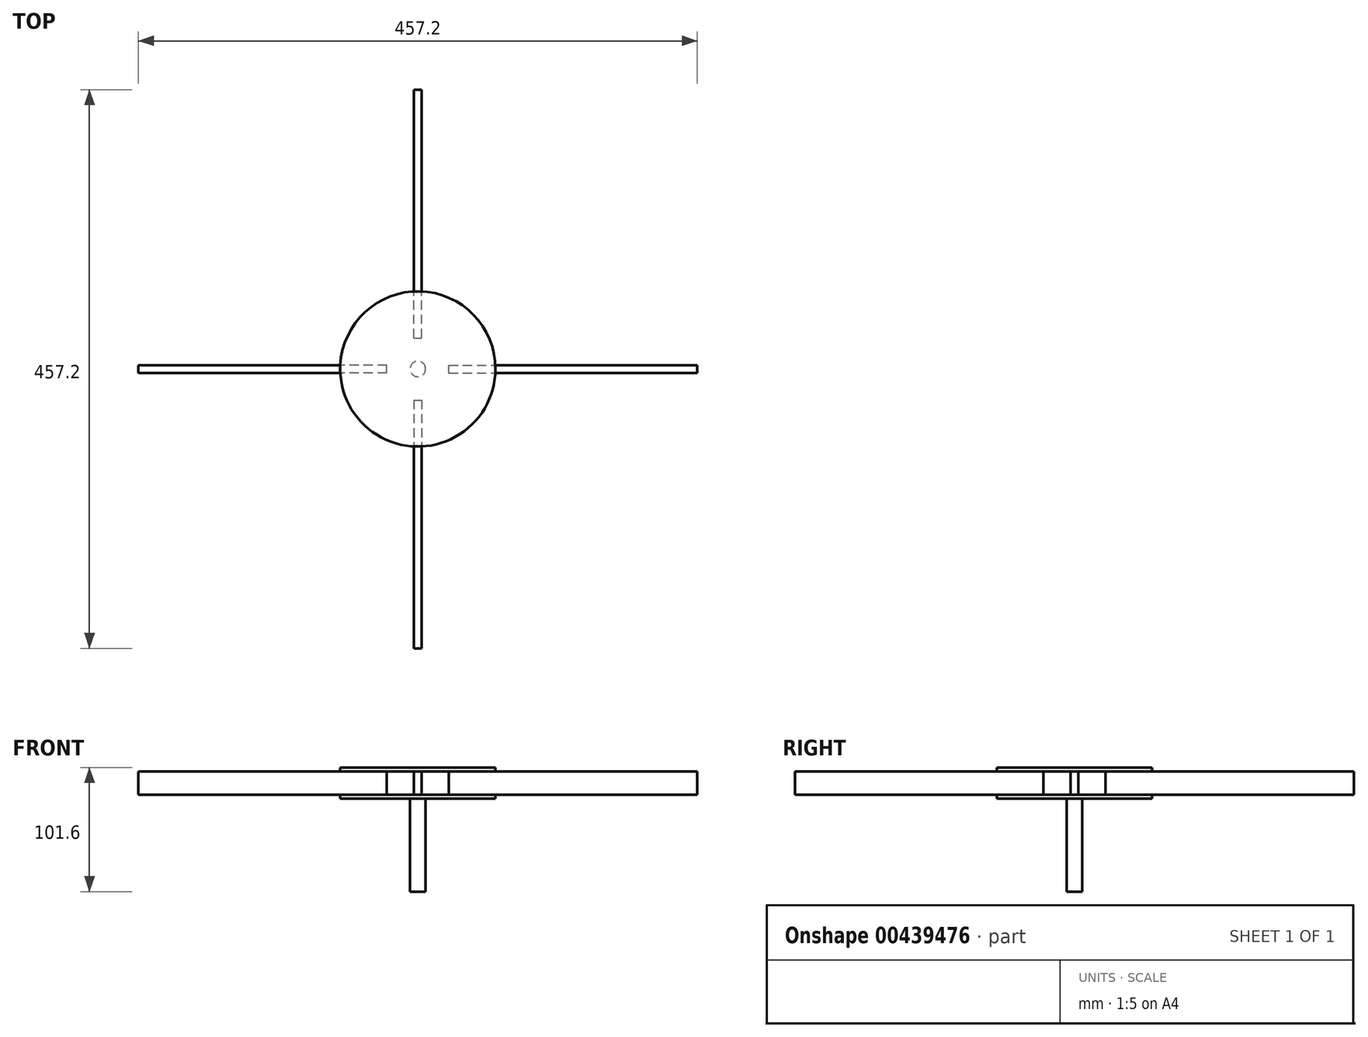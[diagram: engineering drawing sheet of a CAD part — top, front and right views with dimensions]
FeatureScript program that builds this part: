
annotation { "Feature Type Name" : "Feature", "Feature Type Description" : "" }
export const myFeature = defineFeature(function(context is Context, id is Id, definition is map)
    precondition{}
    {
        {
            var Q0;
            Q0=qCreatedBy(makeId("Top.planeOp"),FACE);
            var sketch = newSketch(context, id + "F0", { "sketchPlane" : qUnion([Q0])});
            skCircle(sketch, "E0", {"center": v(0, 0) * mm, "radius": 6.35 * mm});
            skSolve(sketch);
        }
        {
            var Q0;
            Q0=makeQuery(id+"F0.imprint","IMPRINT",FACE,{"disambiguationData":[TD([[makeQuery(id+"F0.imprint","IMPRINT",EDGE,{"derivedFrom":sQuery(id+"F0.wireOp",EDGE,"E0")}),1.0]])]});
            extrude(context, id + "F1", {"entities" : qUnion([Q0]), "endBound" : BoundingType.SYMMETRIC, "depth" : 76.2 * mm});
        }
        {
            var Q0;
            Q0=makeQuery(id+"F1.opExtrude","CAP_FACE",FACE,{"disambiguationData":[OSD([sQuery(id+"F0.wireOp",EDGE,"E0")])],"isStart":false});
            var sketch = newSketch(context, id + "F2", { "sketchPlane" : qUnion([Q0])});
            skCircle(sketch, "E1", {"center": v(0, 0) * mm, "radius": 63.5 * mm});
            skSolve(sketch);
        }
        {
            var Q0;
            Q0 = qSketchRegion(id + "F2", true);
            extrude(context, id + "F3", {"entities" : qUnion([Q0]), "operationType" : NewBodyOperationType.ADD, "depth" : 3.17 * mm});
        }
        {
            var Q0;
            Q0=makeQuery(id+"F3.opExtrude","CAP_FACE",FACE,{"disambiguationData":[OSD([sQuery(id+"F2.wireOp",EDGE,"E1")])],"isStart":false});
            var sketch = newSketch(context, id + "F4", { "sketchPlane" : qUnion([Q0])});
            skLineSegment(sketch, "E2.bottom", {"start": v(-3.17, 25.4) * mm, "end": v(3.18, 25.4) * mm});
            skLineSegment(sketch, "E2.top", {"start": v(-3.18, 228.6) * mm, "end": v(3.17, 228.6) * mm});
            skLineSegment(sketch, "E2.left", {"start": v(-3.17, 25.4) * mm, "end": v(-3.18, 228.6) * mm});
            skLineSegment(sketch, "E2.right", {"start": v(3.18, 25.4) * mm, "end": v(3.17, 228.6) * mm});
            skLineSegment(sketch, "E3.bottom", {"start": v(-25.4, -3.18) * mm, "end": v(-228.6, -3.18) * mm});
            skLineSegment(sketch, "E3.top", {"start": v(-25.4, 3.17) * mm, "end": v(-228.6, 3.17) * mm});
            skLineSegment(sketch, "E3.left", {"start": v(-25.4, -3.18) * mm, "end": v(-25.4, 3.17) * mm});
            skLineSegment(sketch, "E3.right", {"start": v(-228.6, -3.18) * mm, "end": v(-228.6, 3.17) * mm});
            skLineSegment(sketch, "E4", {"start": v(0, 63.5) * mm, "end": v(0, -63.5) * mm, "construction": true});
            skLineSegment(sketch, "E5", {"start": v(63.5, 0) * mm, "end": v(-63.5, 0) * mm, "construction": true});
            skPoint(sketch, "E6", {"position": v(-25.4, 0) * mm});
            skPoint(sketch, "E7", {"position": v(0, 25.4) * mm});
            skLineSegment(sketch, "E8.MirrorCS", {"start": v(25.4, -3.18) * mm, "end": v(25.4, 3.17) * mm});
            skLineSegment(sketch, "E9.MirrorCS", {"start": v(228.6, -3.17) * mm, "end": v(228.6, 3.18) * mm});
            skLineSegment(sketch, "E10.MirrorCS", {"start": v(25.4, 3.17) * mm, "end": v(228.6, 3.17) * mm});
            skLineSegment(sketch, "E11.MirrorCS", {"start": v(25.4, -3.18) * mm, "end": v(228.6, -3.18) * mm});
            skPoint(sketch, "E12.MirrorP", {"position": v(25.4, 0) * mm});
            skLineSegment(sketch, "E13.MirrorCS", {"start": v(-3.17, -25.4) * mm, "end": v(3.18, -25.4) * mm});
            skLineSegment(sketch, "E14.MirrorCS", {"start": v(-3.17, -228.6) * mm, "end": v(3.18, -228.6) * mm});
            skPoint(sketch, "E15.MirrorP", {"position": v(0, -25.4) * mm});
            skLineSegment(sketch, "E16.MirrorCS", {"start": v(3.18, -25.4) * mm, "end": v(3.17, -228.6) * mm});
            skLineSegment(sketch, "E17.MirrorCS", {"start": v(-3.17, -25.4) * mm, "end": v(-3.18, -228.6) * mm});
            skSolve(sketch);
        }
        {
            var Q0;
            Q0 = qSketchRegion(id + "F4", true);
            extrude(context, id + "F5", {"entities" : qUnion([Q0]), "operationType" : NewBodyOperationType.ADD, "depth" : 19.05 * mm});
        }
        {
            var Q0;
            Q0=makeQuery(id+"F5.opExtrude","CAP_FACE",FACE,{"disambiguationData":[OSD([sQuery(id+"F4.wireOp",EDGE,"E13.MirrorCS"),sQuery(id+"F4.wireOp",EDGE,"E14.MirrorCS"),sQuery(id+"F4.wireOp",EDGE,"E16.MirrorCS"),sQuery(id+"F4.wireOp",EDGE,"E17.MirrorCS")])],"isStart":false});
            var sketch = newSketch(context, id + "F6", { "sketchPlane" : qUnion([Q0])});
            skCircle(sketch, "E18", {"center": v(0, 0) * mm, "radius": 63.5 * mm});
            skSolve(sketch);
        }
        {
            var Q0;
            Q0 = qSketchRegion(id + "F6", true);
            extrude(context, id + "F7", {"entities" : qUnion([Q0]), "operationType" : NewBodyOperationType.ADD, "depth" : 3.17 * mm});
        }
    });
